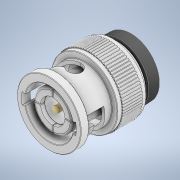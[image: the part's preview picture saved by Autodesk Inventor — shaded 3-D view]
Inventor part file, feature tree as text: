
AUTODESK INVENTOR PART (.ipt)
format: ipt  version: 2022 (Build 260153000, 153)  size: 1,224,704 bytes
history: native  units: in
note: dims shown in document units (in); Inventor stores cm internally (conversion verified against a paired STEP export)
features: other x4, extrude x2, sketch x2, plane x1, fillet x1
ambient origin geometry x8: Origin, YZ Plane, XZ Plane, XY Plane, X Axis, Y Axis, Z Axis, Center Point
bodies: Solid1 (feature_tree), Solid2 (feature_tree), Solid3 (feature_tree), Solid4 (feature_tree), Solid5 (feature_tree)
feature tree (10):
  plane  "Work Plane1"
  extrude  "Extrusion1"  Depth=1.3563in TaperAngle=0.0deg
  extrude  "Extrusion2"  [1 undecoded]
  sketch  "Sketch2"  dims[d0=-0.6693in d1=1.3563in d2=0.0in]
  sketch  "Sketch3"  dims[d3=1.3563in d4=0.0in]
  other  "Boss-Extrude2"
  other  "Boss-Extrude5"
  other  "Cut-Extrude2"
  fillet  "Fillet5"  [1 undecoded]
  other  "Boss-Extrude7"
note: 2 required parameter values undecoded (feature->parameter linkage not recoverable at this tier; creation-order binding heuristic only, values carry confidence <= 0.55)
